# Revit family: EKF_EE_БоковаяПанельДляВРУ-1UNIT_PROxima
name_source: partatom
category: Электрооборудование
units: mm (PartAtom-declared; Revit-internal decimal feet)

## family parameters
Всегда вертикально = Нет
На основе рабочей плоскости = Да
Общий = Да
При загрузке вырезать с полостями = Нет
Размер круглого соединителя = Использовать диаметр
Тип детали = Силовой щит
Точка расчета площади = Нет

## types (4) — shared parameters
ADSK_Единица измерения = шт.
ADSK_Завод-изготовитель = EKF
ADSK_Количество = 1
ADSK_Марка = Боковая панель
ADSK_Материал = RAL 7035_Сталь
ADSK_Обозначение = Боковая панель
ADSK_Размер_Глубина = 2 мм
D = 10 мм
Изготовитель = EKF
Отступ = 20 мм
Серия номенклатуры = Unit PROxima
Степень защиты IP = -
ТВ = EKF_2
Тип установки = -
zero-valued in all types: ADSK_Масса, Отметка по умолчанию

## per-type parameters (varying)
| type | ADSK_Код изделия | ADSK_Размер_Высота | ADSK_Размер_Ширина | Тип |
| Боковая панель для ВРУ-1 (1800хШх600) Unit S сварного и ЩО-70 EKF PROxima | mb15-07-06m | 1800 мм | 600 мм | 7 мм |
| Боковая панель для ВРУ-1 (2000хШх600) Unit S сварного и ЩО-70 EKF PROxima | mb15-04-06m | 2000 мм | 600 мм | 8 мм |
| Боковая панель для ВРУ-1 и ВРУ-2 (1800хШх450) Unit S сварная EKF PROxima | mb15-07-01m | 1800 мм | 450 мм | 9 мм |
| Боковая панель для ВРУ-1 и ВРУ-2 (2000хШх450) Unit S сварная EKF PROxima | mb15-04-01m | 2000 мм | 450 мм | 10 мм |

note: column(s) folded — value = type name in every type: ADSK_Наименование
